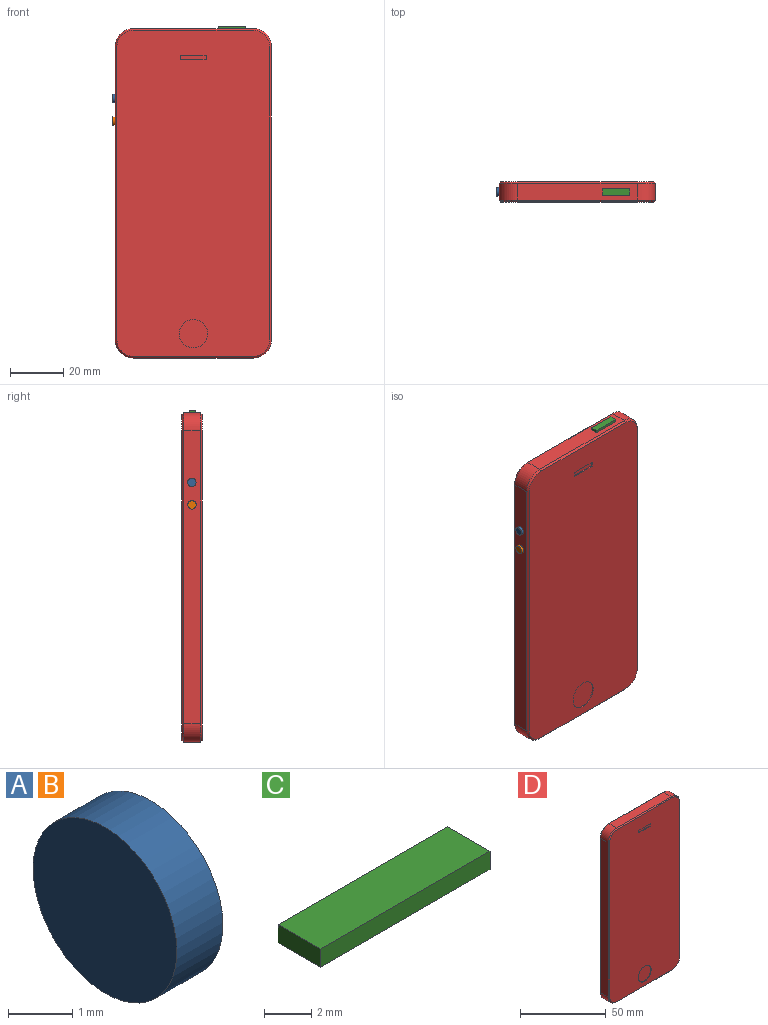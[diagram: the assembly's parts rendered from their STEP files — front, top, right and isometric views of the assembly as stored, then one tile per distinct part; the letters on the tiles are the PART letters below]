
ASSEMBLY  parts=4 mates=3
PART A: 3 faces, bbox 1x3.2x3.2 mm
  f0: cylinder r=1.59mm len=3.18mm, axis (-1,0,0), area 10.1mm2, adj f1,f2
  f1: plane 3.18x3.18mm, normal (1,0,0), area 7.9mm2, adj f0
  f2: plane 3.18x3.18mm, normal (-1,0,0), area 7.9mm2, adj f0
PART B: same geometry as A
PART C: 6 faces, bbox 10.2x2.5x0.9 mm
  f0: plane 10.16x0.94mm, normal (0,1,0), area 9.5mm2, adj f1,f3,f4,f5
  f1: plane 2.54x0.94mm, normal (-1,0,0), area 2.4mm2, adj f0,f2,f4,f5
  f2: plane 10.16x0.94mm, normal (0,-1,0), area 9.5mm2, adj f1,f3,f4,f5
  f3: plane 2.54x0.94mm, normal (1,0,0), area 2.4mm2, adj f0,f2,f4,f5
  f4: plane 10.16x2.54mm, normal (0,0,1), area 25.8mm2, adj f0,f1,f2,f3
  f5: plane 10.16x2.54mm, normal (0,0,-1), area 25.8mm2, adj f0,f1,f2,f3
PART D: 40 faces, bbox 58.7x7.6x123.7 mm
  f0: plane 44.96x6.35mm, normal (0,0,-1), area 260.3mm2, adj f7,f8,f16,f20,f33,f34,f35,f36
  f1: plane 122.43x57.4mm, normal (0,-1,0), area 6888.3mm2, adj f18,f19,f20,f21,f22,f23,f24,f25
  f2: plane 44.96x6.35mm, normal (0,0,1), area 285.5mm2, adj f6,f9,f11,f23
  f3: plane 109.98x6.35mm, normal (-1,0,0), area 698.4mm2, adj f6,f7,f12,f24
  f4: plane 109.98x6.35mm, normal (1,0,0), area 698.4mm2, adj f8,f9,f15,f19
  f5: plane 122.43x57.4mm, normal (0,1,0), area 6994.6mm2, adj f10,f11,f12,f13,f14,f15,f16,f17
  f6: cylinder r=6.86mm len=6.86mm, axis (0,-1,0), area 68.4mm2, adj f2,f3,f10,f25
  f7: cylinder r=6.86mm len=6.86mm, axis (0,1,0), area 68.4mm2, adj f0,f3,f14,f22
  f8: cylinder r=6.86mm len=6.86mm, axis (0,-1,0), area 68.4mm2, adj f0,f4,f17,f18
  f9: cylinder r=6.86mm len=6.86mm, axis (0,1,0), area 68.4mm2, adj f2,f4,f13,f21
  f10: cone r=6.22mm half-angle=45deg, axis (0,-1,0), area 9.2mm2, adj f5,f6,f11,f12
  f11: plane 44.96x0.64mm, normal (0,0.71,0.71), area 40.4mm2, adj f2,f5,f10,f13
  f12: plane 109.98x0.64mm, normal (-0.71,0.71,0), area 98.8mm2, adj f3,f5,f10,f14
  f13: cone r=6.22mm half-angle=45deg, axis (0,-1,0), area 9.2mm2, adj f5,f9,f11,f15
  f14: cone r=6.22mm half-angle=45deg, axis (0,-1,0), area 9.2mm2, adj f5,f7,f12,f16
  f15: plane 109.98x0.64mm, normal (0.71,0.71,0), area 98.8mm2, adj f4,f5,f13,f17
  f16: plane 44.96x0.64mm, normal (0,0.71,-0.71), area 40.4mm2, adj f0,f5,f14,f17
  f17: cone r=6.22mm half-angle=45deg, axis (0,-1,0), area 9.2mm2, adj f5,f8,f15,f16
  f18: cone r=6.22mm half-angle=45deg, axis (0,1,0), area 9.2mm2, adj f1,f8,f19,f20
  f19: plane 109.98x0.64mm, normal (0.71,-0.71,0), area 98.8mm2, adj f1,f4,f18,f21
  f20: plane 44.96x0.64mm, normal (0,-0.71,-0.71), area 40.4mm2, adj f0,f1,f18,f22
  f21: cone r=6.22mm half-angle=45deg, axis (0,1,0), area 9.2mm2, adj f1,f9,f19,f23
  f22: cone r=6.22mm half-angle=45deg, axis (0,1,0), area 9.2mm2, adj f1,f7,f20,f24
  f23: plane 44.96x0.64mm, normal (0,-0.71,0.71), area 40.4mm2, adj f1,f2,f21,f25
  f24: plane 109.98x0.64mm, normal (-0.71,-0.71,0), area 98.8mm2, adj f1,f3,f22,f25
  f25: cone r=6.22mm half-angle=45deg, axis (0,1,0), area 9.2mm2, adj f1,f6,f23,f24
  f26: cylinder r=5.33mm len=10.67mm, axis (0,-1,0), area 12.8mm2, adj f1,f27
  f27: plane 10.67x10.67mm, normal (0,-1,0), area 89.4mm2, adj f26
  f28: plane 9.53x0.38mm, normal (0,0,-1), area 3.6mm2, adj f1,f29,f31,f32
  f29: plane 1.78x0.38mm, normal (1,0,0), area 0.7mm2, adj f1,f28,f30,f32
  f30: plane 9.53x0.38mm, normal (0,0,1), area 3.6mm2, adj f1,f29,f31,f32
  f31: plane 1.78x0.38mm, normal (-1,0,0), area 0.7mm2, adj f1,f28,f30,f32
  f32: plane 9.53x1.78mm, normal (0,-1,0), area 16.9mm2, adj f28,f29,f30,f31
  f33: plane 6.35x6.11mm, normal (0,1,0), area 38.8mm2, adj f0,f34,f36,f37
  f34: plane 6.35x1.25mm, normal (1,0,0), area 7.9mm2, adj f0,f33,f35,f37
  f35: plane 6.35x6.11mm, normal (0,-1,0), area 38.8mm2, adj f0,f34,f36,f37
  f36: plane 6.35x1.25mm, normal (-1,0,0), area 7.9mm2, adj f0,f33,f35,f37
  f37: plane 6.11x1.25mm, normal (0,0,-1), area 7.6mm2, adj f33,f34,f35,f36
  f38: cylinder r=2.36mm len=13.97mm, axis (0,0,-1), area 207.2mm2, adj f0,f39
  f39: plane 4.72x4.72mm, normal (0,0,-1), area 17.5mm2, adj f38
PLACE A t=(-34.07,2.6,37.35)mm
PLACE B t=(-34.07,2.52,28.9)mm
PLACE C t=(10.84,2.37,63.57)mm
PLACE D t=(-3.71,6.33,1.72)mm
MATE planar C.f5 <-> D.f2  axis (0,0,-1) through (10.84,2.37,63.57)mm
MATE planar A.f0 <-> D.f3  axis (1,0,0) through (-33.05,2.6,37.35)mm
MATE planar B.f0 <-> D.f3  axis (1,0,0) through (-33.05,2.52,28.9)mm
